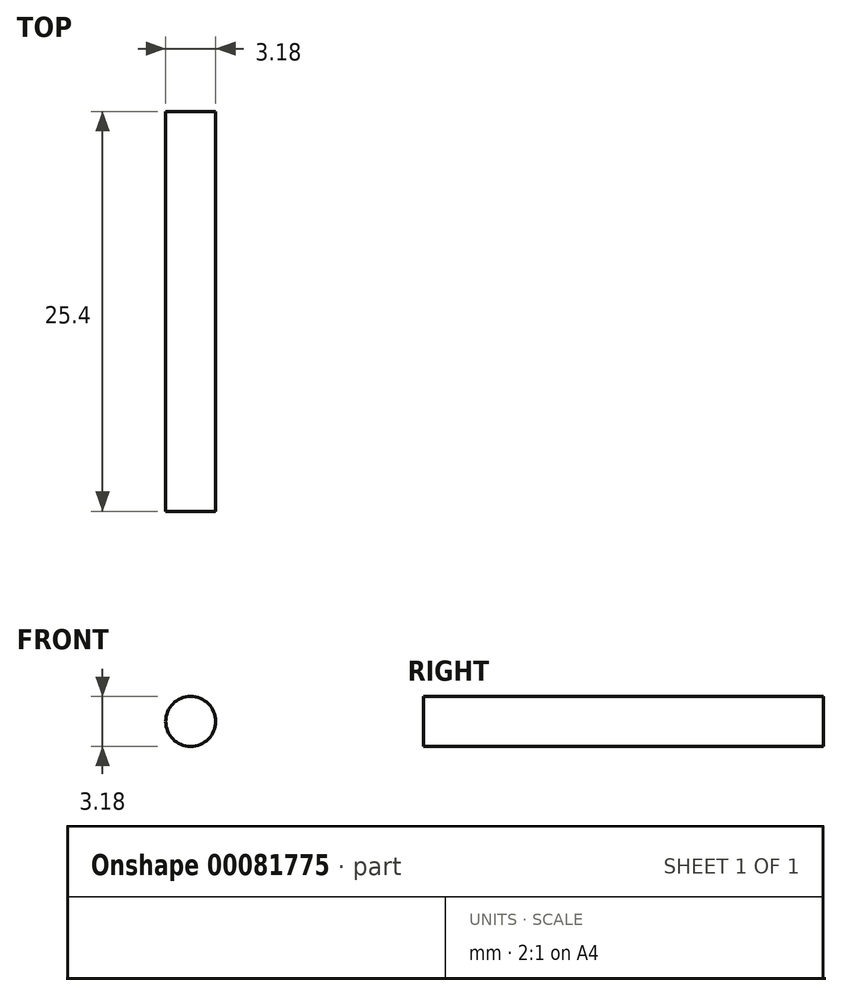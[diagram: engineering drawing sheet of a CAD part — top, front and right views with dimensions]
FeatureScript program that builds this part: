
annotation { "Feature Type Name" : "Feature", "Feature Type Description" : "" }
export const myFeature = defineFeature(function(context is Context, id is Id, definition is map)
    precondition{}
    {
        {
            var Q0;
            Q0=qCreatedBy(makeId("Front.planeOp"),FACE);
            var sketch = newSketch(context, id + "F0", { "sketchPlane" : qUnion([Q0])});
            skCircle(sketch, "E0", {"center": v(0, 0) * mm, "radius": 1.59 * mm});
            skSolve(sketch);
        }
        {
            var Q0;
            Q0=makeQuery(id+"F0.imprint","IMPRINT",FACE,{"disambiguationData":[TD([[makeQuery(id+"F0.imprint","IMPRINT",EDGE,{"derivedFrom":sQuery(id+"F0.wireOp",EDGE,"E0")}),1.0]])]});
            extrude(context, id + "F1", {"entities" : qUnion([Q0]), "depth" : 25.4 * mm});
        }
    });
